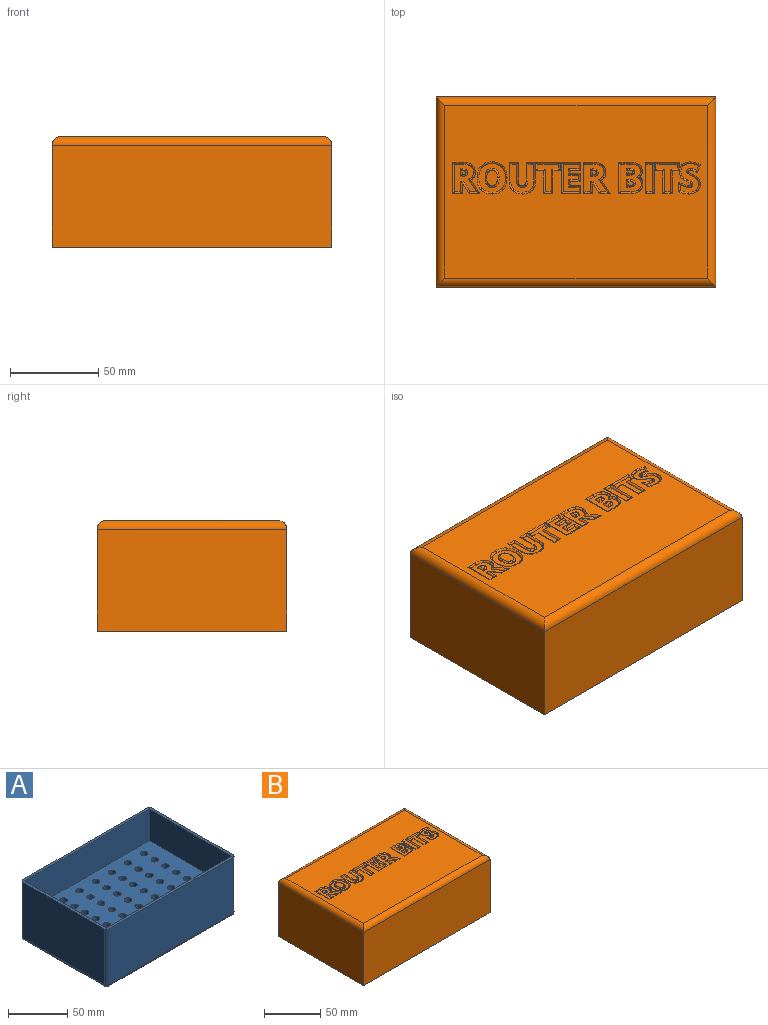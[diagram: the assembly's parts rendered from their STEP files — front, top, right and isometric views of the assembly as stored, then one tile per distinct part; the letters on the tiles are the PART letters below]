
ASSEMBLY  parts=2 mates=1
PART A: 121 faces, bbox 153x102x59.9 mm
  f0: plane 148x57.4mm, normal (0,1,0), area 8495.2mm2, adj f58,f109,f110,f111
  f1: plane 97x57.4mm, normal (-1,0,0), area 5567.8mm2, adj f58,f111,f116,f117
  f2: plane 148x57.4mm, normal (0,-1,0), area 8495.2mm2, adj f58,f114,f117,f120
  f3: cylinder r=3.17mm len=25mm, axis (0,0,-1), area 498.7mm2, adj f53,f107
  f4: cylinder r=3.17mm len=25mm, axis (0,0,-1), area 498.7mm2, adj f53,f106
  f5: cylinder r=3.17mm len=25mm, axis (0,0,-1), area 498.7mm2, adj f53,f105
  f6: cylinder r=3.17mm len=25mm, axis (0,0,-1), area 498.7mm2, adj f53,f104
  f7: cylinder r=3.17mm len=25mm, axis (0,0,-1), area 498.7mm2, adj f53,f103
  f8: cylinder r=3.17mm len=25mm, axis (0,0,-1), area 498.7mm2, adj f53,f102
  f9: cylinder r=3.17mm len=25mm, axis (0,0,-1), area 498.7mm2, adj f53,f101
  f10: cylinder r=3.17mm len=25mm, axis (0,0,-1), area 498.7mm2, adj f53,f100
  f11: cylinder r=3.17mm len=25mm, axis (0,0,-1), area 498.7mm2, adj f53,f99
  f12: cylinder r=3.17mm len=25mm, axis (0,0,-1), area 498.7mm2, adj f53,f98
  f13: cylinder r=3.17mm len=25mm, axis (0,0,-1), area 498.7mm2, adj f53,f97
  f14: cylinder r=3.17mm len=25mm, axis (0,0,-1), area 498.7mm2, adj f53,f96
  f15: cylinder r=3.17mm len=25mm, axis (0,0,-1), area 498.7mm2, adj f53,f95
  f16: cylinder r=3.17mm len=25mm, axis (0,0,-1), area 498.7mm2, adj f53,f94
  f17: cylinder r=3.17mm len=25mm, axis (0,0,-1), area 498.7mm2, adj f53,f93
  f18: cylinder r=3.17mm len=25mm, axis (0,0,-1), area 498.7mm2, adj f53,f92
  f19: cylinder r=3.17mm len=25mm, axis (0,0,-1), area 498.7mm2, adj f53,f91
  f20: cylinder r=3.17mm len=25mm, axis (0,0,-1), area 498.7mm2, adj f53,f90
  f21: cylinder r=3.17mm len=25mm, axis (0,0,-1), area 498.7mm2, adj f53,f89
  f22: cylinder r=3.17mm len=25mm, axis (0,0,-1), area 498.7mm2, adj f53,f88
  f23: cylinder r=3.17mm len=25mm, axis (0,0,-1), area 498.7mm2, adj f53,f87
  f24: cylinder r=3.17mm len=25mm, axis (0,0,-1), area 498.7mm2, adj f53,f86
  f25: cylinder r=3.17mm len=25mm, axis (0,0,-1), area 498.7mm2, adj f53,f85
  f26: cylinder r=3.17mm len=25mm, axis (0,0,-1), area 498.7mm2, adj f53,f84
  f27: cylinder r=3.17mm len=25mm, axis (0,0,-1), area 498.7mm2, adj f53,f83
  f28: cylinder r=3.17mm len=25mm, axis (0,0,-1), area 498.7mm2, adj f53,f82
  f29: cylinder r=3.17mm len=25mm, axis (0,0,-1), area 498.7mm2, adj f53,f81
  f30: cylinder r=3.17mm len=25mm, axis (0,0,-1), area 498.7mm2, adj f53,f80
  f31: cylinder r=3.17mm len=25mm, axis (0,0,-1), area 498.7mm2, adj f53,f79
  f32: cylinder r=3.17mm len=25mm, axis (0,0,-1), area 498.7mm2, adj f53,f78
  f33: cylinder r=3.17mm len=25mm, axis (0,0,-1), area 498.7mm2, adj f53,f77
  f34: cylinder r=3.17mm len=25mm, axis (0,0,-1), area 498.7mm2, adj f53,f76
  f35: cylinder r=3.17mm len=25mm, axis (0,0,-1), area 498.7mm2, adj f53,f75
  f36: cylinder r=3.17mm len=25mm, axis (0,0,-1), area 498.7mm2, adj f53,f74
  f37: cylinder r=3.17mm len=25mm, axis (0,0,-1), area 498.7mm2, adj f53,f73
  f38: cylinder r=3.17mm len=25mm, axis (0,0,-1), area 498.7mm2, adj f53,f72
  f39: cylinder r=3.17mm len=25mm, axis (0,0,-1), area 498.7mm2, adj f53,f71
  f40: cylinder r=3.17mm len=25mm, axis (0,0,-1), area 498.7mm2, adj f53,f70
  f41: cylinder r=3.17mm len=25mm, axis (0,0,-1), area 498.7mm2, adj f53,f69
  f42: cylinder r=3.17mm len=25mm, axis (0,0,-1), area 498.7mm2, adj f53,f68
  f43: cylinder r=3.17mm len=25mm, axis (0,0,-1), area 498.7mm2, adj f53,f67
  f44: cylinder r=3.17mm len=25mm, axis (0,0,-1), area 498.7mm2, adj f53,f66
  f45: cylinder r=3.17mm len=25mm, axis (0,0,-1), area 498.7mm2, adj f53,f65
  f46: cylinder r=3.17mm len=25mm, axis (0,0,-1), area 498.7mm2, adj f53,f64
  f47: cylinder r=3.17mm len=25mm, axis (0,0,-1), area 498.7mm2, adj f53,f63
  f48: cylinder r=3.17mm len=25mm, axis (0,0,-1), area 498.7mm2, adj f53,f62
  f49: cylinder r=3.17mm len=25mm, axis (0,0,-1), area 498.7mm2, adj f53,f61
  f50: cylinder r=3.17mm len=25mm, axis (0,0,-1), area 498.7mm2, adj f53,f60
  f51: cylinder r=3.17mm len=25mm, axis (0,0,-1), area 498.7mm2, adj f53,f59
  f52: plane 97x57.4mm, normal (1,0,0), area 5567.8mm2, adj f58,f109,f114,f115
  f53: plane 148.2x97.2mm, normal (0,0,1), area 12853.2mm2, adj f3,f4,f5,f6,f7,f8,f9,f10
  f54: plane 148.2x32.5mm, normal (0,-1,0), area 4816.5mm2, adj f53,f55,f57,f58
  f55: plane 97.2x32.5mm, normal (-1,0,0), area 3159mm2, adj f53,f54,f56,f58
  f56: plane 148.2x32.5mm, normal (0,1,0), area 4816.5mm2, adj f53,f55,f57,f58
  f57: plane 97.2x32.5mm, normal (1,0,0), area 3159mm2, adj f53,f54,f56,f58
  f58: plane 153x102mm, normal (0,0,1), area 1195.6mm2, adj f0,f1,f2,f52,f54,f55,f56,f57
  f59: plane 6.35x6.35mm, normal (0,0,1), area 31.7mm2, adj f51
  f60: plane 6.35x6.35mm, normal (0,0,1), area 31.7mm2, adj f50
  f61: plane 6.35x6.35mm, normal (0,0,1), area 31.7mm2, adj f49
  f62: plane 6.35x6.35mm, normal (0,0,1), area 31.7mm2, adj f48
  f63: plane 6.35x6.35mm, normal (0,0,1), area 31.7mm2, adj f47
  f64: plane 6.35x6.35mm, normal (0,0,1), area 31.7mm2, adj f46
  f65: plane 6.35x6.35mm, normal (0,0,1), area 31.7mm2, adj f45
  f66: plane 6.35x6.35mm, normal (0,0,1), area 31.7mm2, adj f44
  f67: plane 6.35x6.35mm, normal (0,0,1), area 31.7mm2, adj f43
  f68: plane 6.35x6.35mm, normal (0,0,1), area 31.7mm2, adj f42
  f69: plane 6.35x6.35mm, normal (0,0,1), area 31.7mm2, adj f41
  f70: plane 6.35x6.35mm, normal (0,0,1), area 31.7mm2, adj f40
  f71: plane 6.35x6.35mm, normal (0,0,1), area 31.7mm2, adj f39
  f72: plane 6.35x6.35mm, normal (0,0,1), area 31.7mm2, adj f38
  f73: plane 6.35x6.35mm, normal (0,0,1), area 31.7mm2, adj f37
  f74: plane 6.35x6.35mm, normal (0,0,1), area 31.7mm2, adj f36
  f75: plane 6.35x6.35mm, normal (0,0,1), area 31.7mm2, adj f35
  f76: plane 6.35x6.35mm, normal (0,0,1), area 31.7mm2, adj f34
  f77: plane 6.35x6.35mm, normal (0,0,1), area 31.7mm2, adj f33
  f78: plane 6.35x6.35mm, normal (0,0,1), area 31.7mm2, adj f32
  f79: plane 6.35x6.35mm, normal (0,0,1), area 31.7mm2, adj f31
  f80: plane 6.35x6.35mm, normal (0,0,1), area 31.7mm2, adj f30
  f81: plane 6.35x6.35mm, normal (0,0,1), area 31.7mm2, adj f29
  f82: plane 6.35x6.35mm, normal (0,0,1), area 31.7mm2, adj f28
  f83: plane 6.35x6.35mm, normal (0,0,1), area 31.7mm2, adj f27
  f84: plane 6.35x6.35mm, normal (0,0,1), area 31.7mm2, adj f26
  f85: plane 6.35x6.35mm, normal (0,0,1), area 31.7mm2, adj f25
  f86: plane 6.35x6.35mm, normal (0,0,1), area 31.7mm2, adj f24
  f87: plane 6.35x6.35mm, normal (0,0,1), area 31.7mm2, adj f23
  f88: plane 6.35x6.35mm, normal (0,0,1), area 31.7mm2, adj f22
  f89: plane 6.35x6.35mm, normal (0,0,1), area 31.7mm2, adj f21
  f90: plane 6.35x6.35mm, normal (0,0,1), area 31.7mm2, adj f20
  f91: plane 6.35x6.35mm, normal (0,0,1), area 31.7mm2, adj f19
  f92: plane 6.35x6.35mm, normal (0,0,1), area 31.7mm2, adj f18
  f93: plane 6.35x6.35mm, normal (0,0,1), area 31.7mm2, adj f17
  f94: plane 6.35x6.35mm, normal (0,0,1), area 31.7mm2, adj f16
  f95: plane 6.35x6.35mm, normal (0,0,1), area 31.7mm2, adj f15
  f96: plane 6.35x6.35mm, normal (0,0,1), area 31.7mm2, adj f14
  f97: plane 6.35x6.35mm, normal (0,0,1), area 31.7mm2, adj f13
  f98: plane 6.35x6.35mm, normal (0,0,1), area 31.7mm2, adj f12
  f99: plane 6.35x6.35mm, normal (0,0,1), area 31.7mm2, adj f11
  f100: plane 6.35x6.35mm, normal (0,0,1), area 31.7mm2, adj f10
  f101: plane 6.35x6.35mm, normal (0,0,1), area 31.7mm2, adj f9
  f102: plane 6.35x6.35mm, normal (0,0,1), area 31.7mm2, adj f8
  f103: plane 6.35x6.35mm, normal (0,0,1), area 31.7mm2, adj f7
  f104: plane 6.35x6.35mm, normal (0,0,1), area 31.7mm2, adj f6
  f105: plane 6.35x6.35mm, normal (0,0,1), area 31.7mm2, adj f5
  f106: plane 6.35x6.35mm, normal (0,0,1), area 31.7mm2, adj f4
  f107: plane 6.35x6.35mm, normal (0,0,1), area 31.7mm2, adj f3
  f108: plane 148x97mm, normal (0,0,-1), area 14356mm2, adj f110,f115,f116,f120
  f109: cylinder r=2.5mm len=57.4mm, axis (0,0,1), area 225.4mm2, adj f0,f52,f58,f112
  f110: cylinder r=2.5mm len=148mm, axis (1,0,0), area 581.2mm2, adj f0,f108,f112,f113
  f111: cylinder r=2.5mm len=57.4mm, axis (0,0,-1), area 225.4mm2, adj f0,f1,f58,f113
  f112: sphere r=2.5mm, area 9.8mm2, adj f109,f110,f115
  f113: sphere r=2.5mm, area 9.8mm2, adj f110,f111,f116
  f114: cylinder r=2.5mm len=57.4mm, axis (0,0,-1), area 225.4mm2, adj f2,f52,f58,f118
  f115: cylinder r=2.5mm len=97mm, axis (0,-1,0), area 380.9mm2, adj f52,f108,f112,f118
  f116: cylinder r=2.5mm len=97mm, axis (0,1,0), area 380.9mm2, adj f1,f108,f113,f119
  f117: cylinder r=2.5mm len=57.4mm, axis (0,0,1), area 225.4mm2, adj f1,f2,f58,f119
  f118: sphere r=2.5mm, area 9.8mm2, adj f114,f115,f120
  f119: sphere r=2.5mm, area 9.8mm2, adj f116,f117,f120
  f120: cylinder r=2.5mm len=148mm, axis (-1,0,0), area 581.2mm2, adj f2,f108,f118,f119
PART B: 182 faces, bbox 159.6x108.6x63.6 mm
  f0: plane 148.8x97.8mm, normal (0,0,1), area 12757.8mm2, adj f11,f12,f13,f14,f31,f32,f33,f34
  f1: plane 158.8x107.8mm, normal (0,0,-1), area 1512.6mm2, adj f2,f3,f4,f5,f6,f7,f8,f9
  f2: plane 158.8x57.8mm, normal (0,1,0), area 9178.6mm2, adj f1,f3,f5,f12
  f3: plane 107.8x57.8mm, normal (-1,0,0), area 6230.8mm2, adj f1,f2,f4,f11
  f4: plane 158.8x57.8mm, normal (0,-1,0), area 9178.6mm2, adj f1,f3,f5,f13
  f5: plane 107.8x57.8mm, normal (1,0,0), area 6230.8mm2, adj f1,f2,f4,f14
  f6: plane 153x59.9mm, normal (0,-1,0), area 9164.7mm2, adj f1,f7,f9,f10
  f7: plane 102x59.9mm, normal (1,0,0), area 6109.8mm2, adj f1,f6,f8,f10
  f8: plane 153x59.9mm, normal (0,1,0), area 9164.7mm2, adj f1,f7,f9,f10
  f9: plane 102x59.9mm, normal (-1,0,0), area 6109.8mm2, adj f1,f6,f8,f10
  f10: plane 153x102mm, normal (0,0,-1), area 15606mm2, adj f6,f7,f8,f9
  f11: cylinder r=5mm len=107.8mm, axis (0,-1,0), area 807.4mm2, adj f0,f3,f12,f13
  f12: cylinder r=5mm len=158.8mm, axis (-1,0,0), area 1207.9mm2, adj f0,f2,f11,f14
  f13: cylinder r=5mm len=158.8mm, axis (1,0,0), area 1207.9mm2, adj f0,f4,f11,f14
  f14: cylinder r=5mm len=107.8mm, axis (0,1,0), area 807.4mm2, adj f0,f5,f12,f13
  f15: plane 16.99x11.06mm, normal (0,0,1), area 93.9mm2, adj f39,f40,f41,f42,f43,f44,f45,f46
  f16: plane 15.78x11.92mm, normal (0,0,1), area 76.7mm2, adj f31,f32,f33,f34,f35,f36,f37,f38
  f17: plane 15.78x3.35mm, normal (0,0,1), area 52.8mm2, adj f67,f68,f69,f70
  f18: plane 0.33x0.12mm, normal (-1,0,0), area 0mm2, adj f19,f77,f78
  f19: plane 16.46x12.38mm, normal (0,0,1), area 135.8mm2, adj f18,f71,f72,f73,f74,f75,f76,f77
  f20: plane 2.52x1.51mm, normal (0,0,1), area 3.5mm2, adj f88,f89,f90,f91,f92,f93,f94
  f21: plane 16.44x13.26mm, normal (0,0,1), area 121.6mm2, adj f95,f96,f97,f98,f99,f100,f101,f102
  f22: plane 2.26x2.18mm, normal (0,0,1), area 4.3mm2, adj f107,f108,f109,f110,f111,f112,f113
  f23: plane 15.78x9.09mm, normal (0,0,1), area 99.1mm2, adj f114,f115,f116,f117,f118,f119,f120,f121
  f24: plane 15.78x11.92mm, normal (0,0,1), area 76.7mm2, adj f126,f127,f128,f129,f130,f131,f132,f133
  f25: plane 16.7x13.65mm, normal (0,0,1), area 113.9mm2, adj f134,f135,f136,f137,f138,f139,f140,f141
  f26: plane 17x15.77mm, normal (0,0,1), area 130.4mm2, adj f149,f150,f151,f152,f153,f154,f155,f156
  f27: plane 16.44x13.26mm, normal (0,0,1), area 121.6mm2, adj f163,f164,f165,f166,f167,f168,f169,f170
  f28: plane 2.26x2.18mm, normal (0,0,1), area 4.3mm2, adj f175,f176,f177,f178,f179,f180,f181
  f29: plane 2.88x2.11mm, normal (0,0,1), area 5.6mm2, adj f71,f72,f73,f74,f75,f76
  f30: plane 8.65x6.01mm, normal (0,0,1), area 43.7mm2, adj f149,f150,f151,f152,f153,f154
  f31: cylinder r=1mm len=14mm, axis (0,1,0), area 20.4mm2, adj f0,f16,f32,f33
  f32: cylinder r=1mm len=5.29mm, axis (-1,0,0), area 6.7mm2, adj f0,f16,f31,f34
  f33: cylinder r=1mm len=5.35mm, axis (-1,0,0), area 6.8mm2, adj f0,f16,f31,f35
  f34: cylinder r=1mm len=4.78mm, axis (0,1,0), area 5.9mm2, adj f0,f16,f32,f36
  f35: cylinder r=1mm len=14mm, axis (0,-1,0), area 20.4mm2, adj f0,f16,f33,f37
  f36: cylinder r=1mm len=13.92mm, axis (1,0,0), area 20.3mm2, adj f0,f16,f34,f38
  f37: cylinder r=1mm len=5.12mm, axis (-1,0,0), area 6.7mm2, adj f0,f16,f35,f38,f40
  f38: cylinder r=1mm len=4.62mm, axis (0,-1,0), area 5.8mm2, adj f0,f16,f36,f37,f40
  f39: bspline ~3.27x1.64mm, area 3.4mm2, adj f0,f15,f40,f41
  f40: bspline ~4.91x3.15mm, area 6.2mm2, adj f0,f15,f37,f38,f39,f42
  f41: bspline ~2.54x2.38mm, area 3.2mm2, adj f0,f15,f39,f43
  f42: bspline ~5.57x2.71mm, area 7mm2, adj f0,f15,f40,f44
  f43: bspline ~3.79x2.84mm, area 4.1mm2, adj f0,f15,f41,f45
  f44: bspline ~3.49x1.4mm, area 3.9mm2, adj f0,f15,f42,f46
  f45: bspline ~3.26x2.32mm, area 3.5mm2, adj f0,f15,f43,f47
  f46: bspline ~5.21x2.76mm, area 4.8mm2, adj f0,f15,f44,f48
  f47: bspline ~1.55x1.54mm, area 1.4mm2, adj f0,f15,f45,f49
  f48: cylinder r=1mm len=4.82mm, axis (-0.38,-0.92,0), area 6mm2, adj f0,f15,f46,f50
  f49: bspline ~1.17x1.11mm, area 1mm2, adj f0,f15,f47,f51
  f50: bspline ~4.52x2.5mm, area 4.2mm2, adj f0,f15,f48,f52
  f51: bspline ~1.65x1.46mm, area 1.7mm2, adj f0,f15,f49,f53
  f52: bspline ~2.03x1.25mm, area 2.4mm2, adj f0,f15,f50,f54
  f53: bspline ~2.57x1.3mm, area 2.4mm2, adj f0,f15,f51,f55
  f54: bspline ~2.23x1.39mm, area 2mm2, adj f0,f15,f52,f56
  f55: bspline ~2.87x1.37mm, area 3.1mm2, adj f0,f15,f53,f57
  f56: bspline ~1.48x1.34mm, area 1.6mm2, adj f0,f15,f54,f58
  f57: bspline ~5.61x3.04mm, area 5.7mm2, adj f0,f15,f55,f59
  f58: bspline ~1.16x1.13mm, area 1mm2, adj f0,f15,f56,f60
  f59: cylinder r=1mm len=5.28mm, axis (0,1,0), area 6.6mm2, adj f0,f15,f57,f61
  f60: bspline ~1.33x1.31mm, area 1.2mm2, adj f0,f15,f58,f62
  f61: bspline ~8.99x3.82mm, area 8mm2, adj f0,f15,f59,f63
  f62: bspline ~3.4x2.39mm, area 3.7mm2, adj f0,f15,f60,f64
  f63: bspline ~6.55x2.81mm, area 7.5mm2, adj f0,f15,f61,f65
  f64: bspline ~4.31x3.48mm, area 6.1mm2, adj f0,f15,f62,f66
  f65: bspline ~5.25x2.71mm, area 6.5mm2, adj f0,f15,f63,f66
  f66: bspline ~4.62x2.13mm, area 4.7mm2, adj f0,f15,f64,f65
  f67: cylinder r=1mm len=5.35mm, axis (1,0,0), area 6.8mm2, adj f0,f17,f68,f69
  f68: cylinder r=1mm len=17.78mm, axis (0,-1,0), area 26.4mm2, adj f0,f17,f67,f70
  f69: cylinder r=1mm len=17.78mm, axis (0,1,0), area 26.4mm2, adj f0,f17,f67,f70
  f70: cylinder r=1mm len=5.35mm, axis (-1,0,0), area 6.8mm2, adj f0,f17,f68,f69
  f71: cylinder r=1mm len=2.07mm, axis (-1,0,0), area 2.5mm2, adj f19,f29,f72,f73
  f72: cylinder r=1mm len=4.11mm, axis (0,-1,0), area 4.9mm2, adj f19,f29,f71,f74
  f73: bspline ~4.63x3.13mm, area 5.2mm2, adj f19,f29,f71,f75
  f74: cylinder r=1mm len=2.18mm, axis (1,0,0), area 2.6mm2, adj f19,f29,f72,f76
  f75: bspline ~2.45x1.63mm, area 2.3mm2, adj f19,f29,f73,f76
  f76: bspline ~3.06x1.54mm, area 3mm2, adj f19,f29,f74,f75
  f77: bspline ~4.11x2.82mm, area 3.2mm2, adj f0,f18,f19,f78,f79
  f78: bspline ~3.17x2.64mm, area 2.5mm2, adj f0,f18,f19,f77,f80
  f79: bspline ~4.43x1.96mm, area 4.4mm2, adj f0,f19,f77,f81
  f80: bspline ~4.2x1.93mm, area 4.2mm2, adj f0,f19,f78,f82
  f81: bspline ~4.96x3.3mm, area 6.6mm2, adj f0,f19,f79,f83
  f82: bspline ~4.43x3.11mm, area 6.2mm2, adj f0,f19,f80,f84
  f83: bspline ~5.97x2.34mm, area 7.4mm2, adj f0,f19,f81,f85
  f84: bspline ~7.17x2.28mm, area 8.2mm2, adj f0,f19,f82,f86
  f85: cylinder r=1mm len=6.9mm, axis (-1,0,0), area 10.1mm2, adj f0,f19,f83,f87
  f86: cylinder r=1mm len=5.91mm, axis (1,0,0), area 8.5mm2, adj f0,f19,f84,f87
  f87: cylinder r=1mm len=17.78mm, axis (0,1,0), area 26.4mm2, adj f0,f19,f85,f86
  f88: bspline ~2.89x1.39mm, area 3.1mm2, adj f19,f20,f89,f90
  f89: bspline ~1.93x1.25mm, area 1.8mm2, adj f19,f20,f88,f91
  f90: cylinder r=1mm len=1.76mm, axis (-1,0,0), area 2mm2, adj f19,f20,f88,f92
  f91: bspline ~1.88x1.38mm, area 1.9mm2, adj f19,f20,f89,f93
  f92: cylinder r=1mm len=3.51mm, axis (0,-1,0), area 3.9mm2, adj f19,f20,f90,f94
  f93: bspline ~2.55x1.49mm, area 2.9mm2, adj f19,f20,f91,f94
  f94: cylinder r=1mm len=1.94mm, axis (1,0,0), area 2.3mm2, adj f19,f20,f92,f93
  f95: bspline ~12.83x9.16mm, area 13.7mm2, adj f0,f21,f96,f97
  f96: cylinder r=1mm len=6.18mm, axis (-1,0,0), area 7.8mm2, adj f0,f21,f95,f98
  f97: bspline ~3.62x3.33mm, area 3.8mm2, adj f0,f21,f95,f99
  f98: cylinder r=1mm len=7.05mm, axis (-0.53,0.85,0), area 11.2mm2, adj f0,f21,f96,f100
  f99: bspline ~3.99x2.06mm, area 4.5mm2, adj f0,f21,f97,f101
  f100: cylinder r=1mm len=1.78mm, axis (-1,0,0), area 1.9mm2, adj f0,f21,f98,f102
  f101: bspline ~5.2x3.33mm, area 6.9mm2, adj f0,f21,f99,f103
  f102: cylinder r=1mm len=7.05mm, axis (0,-1,0), area 9.5mm2, adj f0,f21,f100,f104
  f103: bspline ~7.41x2.86mm, area 8.2mm2, adj f0,f21,f101,f105
  f104: cylinder r=1mm len=5.35mm, axis (-1,0,0), area 6.8mm2, adj f0,f21,f102,f106
  f105: cylinder r=1mm len=5.6mm, axis (1,0,0), area 8mm2, adj f0,f21,f103,f106
  f106: cylinder r=1mm len=17.78mm, axis (0,1,0), area 26.4mm2, adj f0,f21,f104,f105
  f107: bspline ~2.16x1.4mm, area 2.3mm2, adj f21,f22,f108,f109
  f108: bspline ~2.49x1.78mm, area 2.4mm2, adj f21,f22,f107,f110
  f109: bspline ~2.81x1.49mm, area 3.6mm2, adj f21,f22,f107,f111
  f110: bspline ~3.55x1.42mm, area 3.5mm2, adj f21,f22,f108,f112
  f111: cylinder r=1mm len=1.02mm, axis (-1,0,0), area 1mm2, adj f21,f22,f109,f113
  f112: cylinder r=1mm len=1.08mm, axis (1,0,0), area 1.1mm2, adj f21,f22,f110,f113
  f113: cylinder r=1mm len=4.26mm, axis (0,-1,0), area 5.1mm2, adj f21,f22,f111,f112
  f114: cylinder r=1mm len=3.46mm, axis (0,-1,0), area 3.9mm2, adj f0,f23,f115,f116
  f115: cylinder r=1mm len=6.34mm, axis (1,0,0), area 8.4mm2, adj f0,f23,f114,f117
  f116: cylinder r=1mm len=6.74mm, axis (-1,0,0), area 9mm2, adj f0,f23,f114,f118
  f117: cylinder r=1mm len=4.74mm, axis (0,-1,0), area 5.9mm2, adj f0,f23,f115,f119
  f118: cylinder r=1mm len=4.74mm, axis (0,-1,0), area 5.9mm2, adj f0,f23,f116,f120
  f119: cylinder r=1mm len=6.34mm, axis (-1,0,0), area 8.4mm2, adj f0,f23,f117,f121
  f120: cylinder r=1mm len=11.09mm, axis (1,0,0), area 15.8mm2, adj f0,f23,f118,f122
  f121: cylinder r=1mm len=4.07mm, axis (0,-1,0), area 4.8mm2, adj f0,f23,f119,f123
  f122: cylinder r=1mm len=17.78mm, axis (0,1,0), area 26.4mm2, adj f0,f23,f120,f124
  f123: cylinder r=1mm len=6.74mm, axis (1,0,0), area 9mm2, adj f0,f23,f121,f125
  f124: cylinder r=1mm len=11.09mm, axis (-1,0,0), area 15.8mm2, adj f0,f23,f122,f125
  f125: cylinder r=1mm len=4.76mm, axis (0,-1,0), area 5.9mm2, adj f0,f23,f123,f124
  f126: cylinder r=1mm len=4.78mm, axis (0,1,0), area 5.9mm2, adj f0,f24,f127,f128
  f127: cylinder r=1mm len=13.92mm, axis (1,0,0), area 20.3mm2, adj f0,f24,f126,f129
  f128: cylinder r=1mm len=5.29mm, axis (-1,0,0), area 6.7mm2, adj f0,f24,f126,f130
  f129: cylinder r=1mm len=4.78mm, axis (0,-1,0), area 5.9mm2, adj f0,f24,f127,f131
  f130: cylinder r=1mm len=14mm, axis (0,1,0), area 20.4mm2, adj f0,f24,f128,f132
  f131: cylinder r=1mm len=5.28mm, axis (-1,0,0), area 6.7mm2, adj f0,f24,f129,f133
  f132: cylinder r=1mm len=5.35mm, axis (-1,0,0), area 6.8mm2, adj f0,f24,f130,f133
  f133: cylinder r=1mm len=14mm, axis (0,-1,0), area 20.4mm2, adj f0,f24,f131,f132
  f134: cylinder r=1mm len=5.33mm, axis (1,0,0), area 6.8mm2, adj f0,f25,f135,f136
  f135: cylinder r=1mm len=11.17mm, axis (0,1,0), area 16.8mm2, adj f0,f25,f134,f137
  f136: cylinder r=1mm len=10.66mm, axis (0,-1,0), area 16mm2, adj f0,f25,f134,f138
  f137: bspline ~7.41x3.73mm, area 7.9mm2, adj f0,f25,f135,f139
  f138: bspline ~3.32x1.82mm, area 4mm2, adj f0,f25,f136,f140
  f139: bspline ~7.91x3.18mm, area 8.4mm2, adj f0,f25,f137,f141
  f140: bspline ~3.92x2mm, area 3.7mm2, adj f0,f25,f138,f142
  f141: bspline ~5.37x2.03mm, area 5.9mm2, adj f0,f25,f139,f143
  f142: bspline ~3.13x2.05mm, area 3.6mm2, adj f0,f25,f140,f144
  f143: bspline ~4.05x3.77mm, area 5.2mm2, adj f0,f25,f141,f145
  f144: bspline ~4.08x1.82mm, area 4.1mm2, adj f0,f25,f142,f146
  f145: bspline ~4.85x2.13mm, area 5.3mm2, adj f0,f25,f143,f147
  f146: cylinder r=1mm len=10.64mm, axis (0,1,0), area 15.9mm2, adj f0,f25,f144,f148
  f147: cylinder r=1mm len=11.21mm, axis (0,-1,0), area 16.8mm2, adj f0,f25,f145,f148
  f148: cylinder r=1mm len=5.34mm, axis (1,0,0), area 6.8mm2, adj f0,f25,f146,f147
  f149: bspline ~5.63x2.36mm, area 6.2mm2, adj f26,f30,f150,f151
  f150: bspline ~5.64x2.36mm, area 6.2mm2, adj f26,f30,f149,f152
  f151: bspline ~3.93x2.1mm, area 4.9mm2, adj f26,f30,f149,f153
  f152: bspline ~3.68x2.56mm, area 4.8mm2, adj f26,f30,f150,f154
  f153: bspline ~8.62x5.63mm, area 11mm2, adj f26,f30,f151,f154
  f154: bspline ~8.61x5.65mm, area 11mm2, adj f26,f30,f152,f153
  f155: bspline ~9x3.81mm, area 10.1mm2, adj f0,f26,f156,f157
  f156: bspline ~8.93x3.82mm, area 10.1mm2, adj f0,f26,f155,f158
  f157: bspline ~10x3.77mm, area 10.6mm2, adj f0,f26,f155,f159
  f158: bspline ~8.21x3.76mm, area 10.6mm2, adj f0,f26,f156,f160
  f159: bspline ~10.08x3.78mm, area 10.6mm2, adj f0,f26,f157,f161
  f160: bspline ~9.37x3.14mm, area 10.6mm2, adj f0,f26,f158,f162
  f161: bspline ~8.94x3.83mm, area 10.1mm2, adj f0,f26,f159,f162
  f162: bspline ~8.94x3.83mm, area 10.1mm2, adj f0,f26,f160,f161
  f163: bspline ~12.83x9.16mm, area 13.7mm2, adj f0,f27,f164,f165
  f164: cylinder r=1mm len=6.18mm, axis (-1,0,0), area 7.8mm2, adj f0,f27,f163,f166
  f165: bspline ~3.62x3.33mm, area 3.8mm2, adj f0,f27,f163,f167
  f166: cylinder r=1mm len=7.05mm, axis (-0.53,0.85,0), area 11.2mm2, adj f0,f27,f164,f168
  f167: bspline ~3.99x2.06mm, area 4.5mm2, adj f0,f27,f165,f169
  f168: cylinder r=1mm len=1.78mm, axis (-1,0,0), area 1.9mm2, adj f0,f27,f166,f170
  f169: bspline ~5.94x3.33mm, area 6.9mm2, adj f0,f27,f167,f171
  f170: cylinder r=1mm len=7.05mm, axis (0,-1,0), area 9.5mm2, adj f0,f27,f168,f172
  f171: bspline ~7.41x2.86mm, area 8.2mm2, adj f0,f27,f169,f173
  f172: cylinder r=1mm len=5.35mm, axis (-1,0,0), area 6.8mm2, adj f0,f27,f170,f174
  f173: cylinder r=1mm len=5.6mm, axis (1,0,0), area 8mm2, adj f0,f27,f171,f174
  f174: cylinder r=1mm len=17.78mm, axis (0,1,0), area 26.4mm2, adj f0,f27,f172,f173
  f175: bspline ~2.31x1.7mm, area 2.3mm2, adj f27,f28,f176,f177
  f176: bspline ~2.3x1.44mm, area 2.4mm2, adj f27,f28,f175,f178
  f177: bspline ~3.27x1.49mm, area 3.6mm2, adj f27,f28,f175,f179
  f178: bspline ~3.81x1.65mm, area 3.5mm2, adj f27,f28,f176,f180
  f179: cylinder r=1mm len=1.02mm, axis (-1,0,0), area 1mm2, adj f27,f28,f177,f181
  f180: cylinder r=1mm len=1.08mm, axis (1,0,0), area 1.1mm2, adj f27,f28,f178,f181
  f181: cylinder r=1mm len=4.26mm, axis (0,-1,0), area 5.1mm2, adj f27,f28,f179,f180
PLACE A t=(-12.32,44.57,3.81)mm fixed
PLACE B t=(-12.32,44.57,3.98)mm
MATE slider A.f28 <-> B.f10  axis (0,0,1) through (-12.32,44.57,28.81)mm
